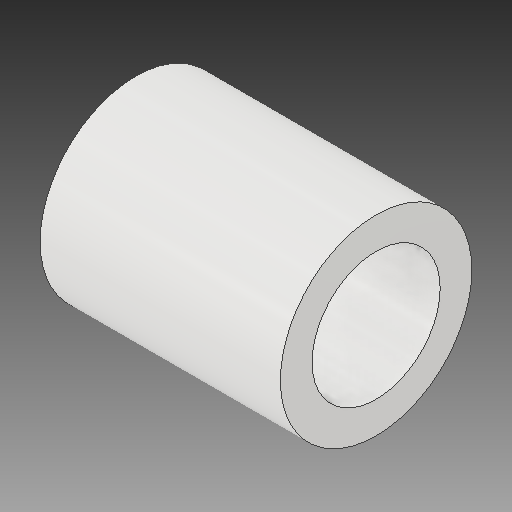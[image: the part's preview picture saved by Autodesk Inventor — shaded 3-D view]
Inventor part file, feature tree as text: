
AUTODESK INVENTOR PART (.ipt)
format: ipt  version: 2017.3 (Build 213256000, 256)  size: 117,248 bytes
history: native  units: mm
features: extrude x3, sketch x3
ambient origin geometry x8: Origin, YZ Plane, XZ Plane, XY Plane, X Axis, Y Axis, Z Axis, Center Point
bodies: Body1 (feature_tree)
feature tree (6):
  extrude  "Extrusion3"  Depth=1.6mm
  extrude  "Extrusion4"  Depth=3.0mm TaperAngle=0.0deg
  extrude  "Extrusion5"  [1 undecoded]
  sketch  "Sketch4"  dims[d12=2.39mm d13=1.6mm]
  sketch  "Sketch5"  dims[d14=3.0mm d15=0.0mm d16=1.0mm d17=0.0mm]
  sketch  "Sketch6"  dims[d18=1.0mm d19=0.0mm]
note: 1 required parameter value undecoded (feature->parameter linkage not recoverable at this tier; creation-order binding heuristic only, values carry confidence <= 0.55)
